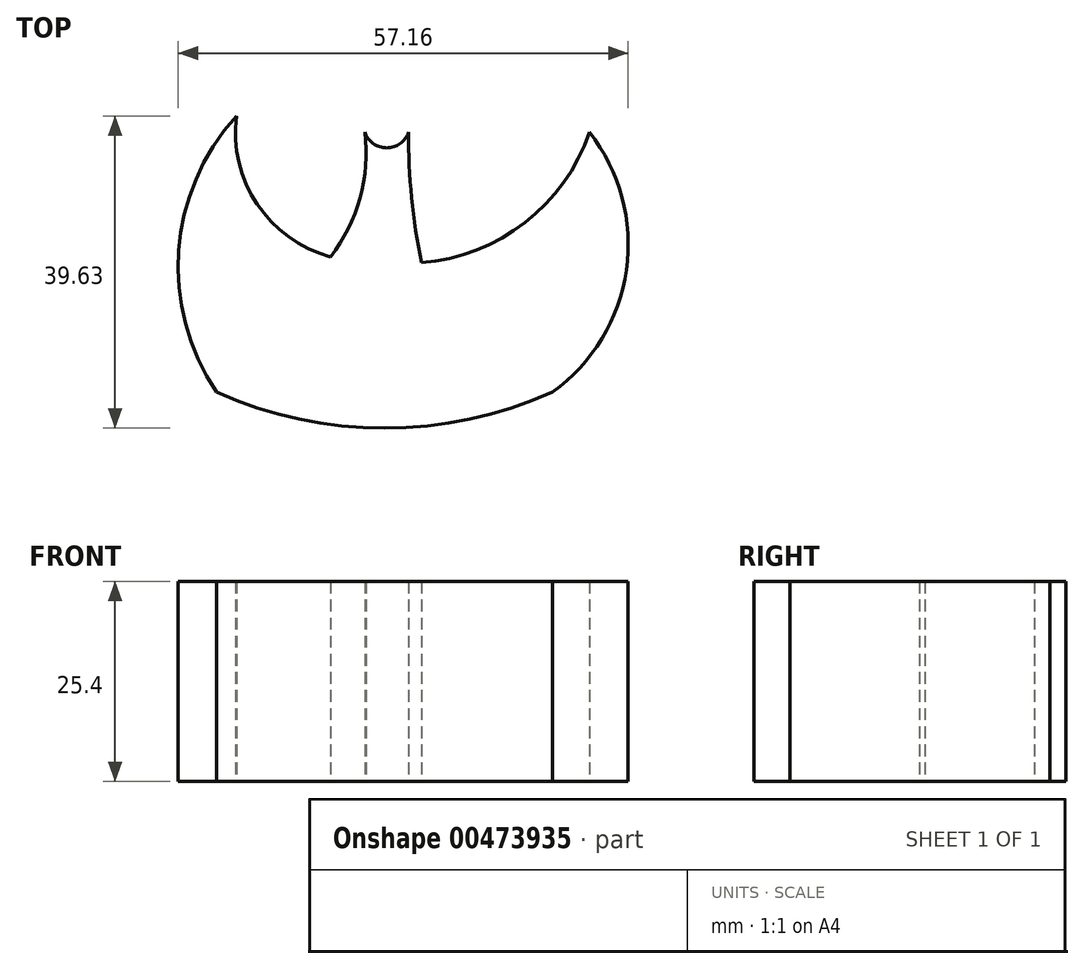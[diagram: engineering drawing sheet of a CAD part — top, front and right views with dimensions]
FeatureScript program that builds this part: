
annotation { "Feature Type Name" : "Feature", "Feature Type Description" : "" }
export const myFeature = defineFeature(function(context is Context, id is Id, definition is map)
    precondition{}
    {
        {
            var Q0;
            Q0=qCreatedBy(makeId("Top.planeOp"),FACE);
            var sketch = newSketch(context, id + "F0", { "sketchPlane" : qUnion([Q0])});
            skArc(sketch, "E0", {"start": v(-17.18, 23.96) * mm, "mid": v(-14.54, 12.78) * mm, "end": v(-5.24, 6.06) * mm});
            skArc(sketch, "E1", {"start": v(-5.24, 6.06) * mm, "mid": v(-1.48, 13.55) * mm, "end": v(-0.87, 21.9) * mm});
            skArc(sketch, "E2", {"start": v(-0.87, 21.9) * mm, "mid": v(1.92, 19.92) * mm, "end": v(4.7, 21.9) * mm});
            skArc(sketch, "E3", {"start": v(4.7, 21.9) * mm, "mid": v(5.08, 13.58) * mm, "end": v(6.33, 5.33) * mm});
            skArc(sketch, "E4", {"start": v(6.33, 5.33) * mm, "mid": v(19.48, 10.43) * mm, "end": v(27.66, 21.9) * mm});
            skArc(sketch, "E5", {"start": v(22.96, -11.12) * mm, "mid": v(32.35, 4.4) * mm, "end": v(27.66, 21.9) * mm});
            skArc(sketch, "E6", {"start": v(-19.7, -11.12) * mm, "mid": v(1.63, -15.67) * mm, "end": v(22.96, -11.12) * mm});
            skArc(sketch, "E7", {"start": v(-17.18, 23.96) * mm, "mid": v(-24.5, 6.86) * mm, "end": v(-19.7, -11.12) * mm});
            skSolve(sketch);
        }
        {
            var Q0;
            Q0 = qSketchRegion(id + "F0", true);
            extrude(context, id + "F1", {"entities" : qUnion([Q0]), "depth" : 25.4 * mm});
        }
    });
